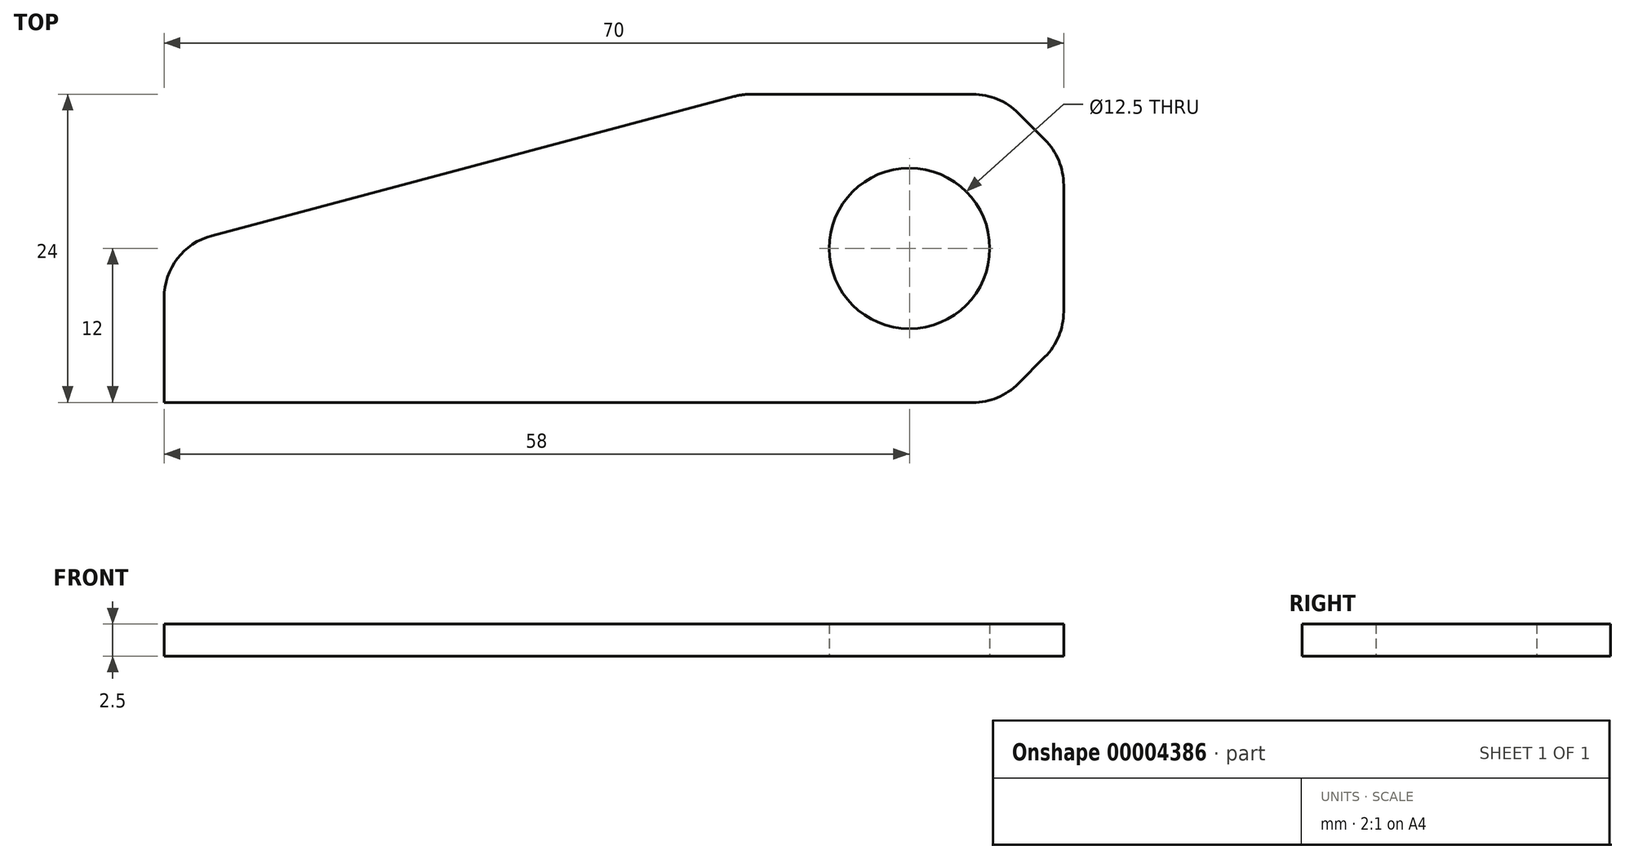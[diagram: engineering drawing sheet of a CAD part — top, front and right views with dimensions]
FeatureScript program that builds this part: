
annotation { "Feature Type Name" : "Feature", "Feature Type Description" : "" }
export const myFeature = defineFeature(function(context is Context, id is Id, definition is map)
    precondition{}
    {
        {
            var Q0;
            Q0=qCreatedBy(makeId("Top.planeOp"),FACE);
            var sketch = newSketch(context, id + "F0", { "sketchPlane" : qUnion([Q0])});
            skLineSegment(sketch, "E0.bottom", {"start": v(-13, 12) * mm, "end": v(7, 12) * mm});
            skLineSegment(sketch, "E0.top", {"start": v(-58, -12) * mm, "end": v(7, -12) * mm});
            skLineSegment(sketch, "E0.left", {"start": v(-58, 0) * mm, "end": v(-58, -12) * mm});
            skLineSegment(sketch, "E0.right", {"start": v(12, 7) * mm, "end": v(12, -7) * mm});
            skCircle(sketch, "E1", {"center": v(0, 0) * mm, "radius": 6.25 * mm});
            skLineSegment(sketch, "E2", {"start": v(-58, 0) * mm, "end": v(-13, 12) * mm});
            skLineSegment(sketch, "E3", {"start": v(7, 12) * mm, "end": v(12, 7) * mm});
            skLineSegment(sketch, "E4", {"start": v(12, -7) * mm, "end": v(7, -12) * mm});
            skSolve(sketch);
        }
        {
            var Q0;
            Q0 = qSketchRegion(id + "F0", true);
            extrude(context, id + "F1", {"entities" : qUnion([Q0]), "depth" : 2.5 * mm});
        }
        {
            var Q0;
            Q0=makeQuery(id+"F1.opExtrude","SWEPT_EDGE",EDGE,{"disambiguationData":[OSD([sQuery(id+"F0.wireOp",EDGE,"E0.left"),sQuery(id+"F0.wireOp",EDGE,"E2")])]});
            var Q1;
            Q1=makeQuery(id+"F1.opExtrude","SWEPT_EDGE",EDGE,{"disambiguationData":[OSD([sQuery(id+"F0.wireOp",EDGE,"E0.bottom"),sQuery(id+"F0.wireOp",EDGE,"E2")])]});
            var Q2;
            Q2=makeQuery(id+"F1.opExtrude","SWEPT_EDGE",EDGE,{"disambiguationData":[OSD([sQuery(id+"F0.wireOp",EDGE,"E0.bottom"),sQuery(id+"F0.wireOp",EDGE,"E3")])]});
            var Q3;
            Q3=makeQuery(id+"F1.opExtrude","SWEPT_EDGE",EDGE,{"disambiguationData":[OSD([sQuery(id+"F0.wireOp",EDGE,"E0.right"),sQuery(id+"F0.wireOp",EDGE,"E3")])]});
            var Q4;
            Q4=makeQuery(id+"F1.opExtrude","SWEPT_EDGE",EDGE,{"disambiguationData":[OSD([sQuery(id+"F0.wireOp",EDGE,"E0.right"),sQuery(id+"F0.wireOp",EDGE,"E4")])]});
            var Q5;
            Q5=makeQuery(id+"F1.opExtrude","SWEPT_EDGE",EDGE,{"disambiguationData":[OSD([sQuery(id+"F0.wireOp",EDGE,"E0.top"),sQuery(id+"F0.wireOp",EDGE,"E4")])]});
            fillet(context, id + "F2", {"entities" : qUnion([Q0, Q1, Q2, Q3, Q4, Q5]), "radius" : 5 * mm, "tangentPropagation" : true, "allowEdgeOverflow" : false});
        }
    });
